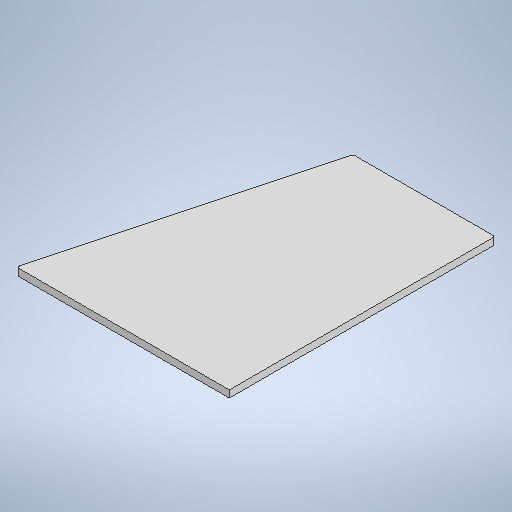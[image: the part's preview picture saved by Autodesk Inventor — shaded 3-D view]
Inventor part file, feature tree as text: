
AUTODESK INVENTOR PART (.ipt)
format: ipt  version: 2025 (Build 290162010, 162A)  size: 257,024 bytes
history: native  units: mm
features: other x2, sheet_metal_op x1, chamfer x1, sketch x1
ambient origin geometry x8: Origin, YZ Plane, XZ Plane, XY Plane, X Axis, Y Axis, Z Axis, Center Point
bodies: Solid1 (feature_tree)
feature tree (5):
  sheet_metal_op  "Face1"
  chamfer  "Corner Round1"
  sketch  "Sketch1"  dims[d2=15.0deg d3=8.0mm d14=2.0mm d29=160.0mm d40=300.0mm d41=15.0deg]
  other  "Plate1"
  other  "Definition1"
